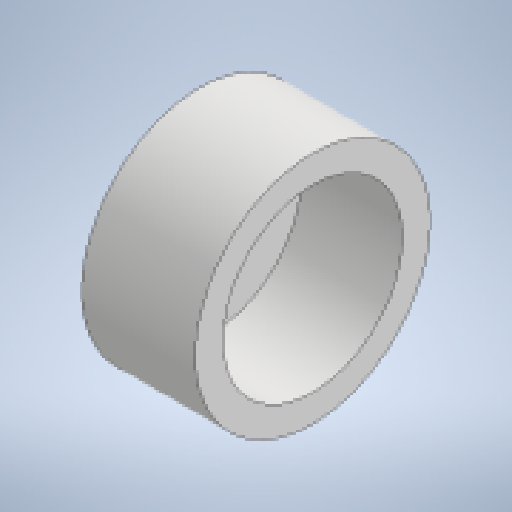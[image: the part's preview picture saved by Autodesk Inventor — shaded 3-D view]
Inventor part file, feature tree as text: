
AUTODESK INVENTOR PART (.ipt)
format: ipt  version: 2023 (Build 270158000, 158)  size: 229,888 bytes
history: native  units: mm
features: extrude x4, sketch x4, other x1
ambient origin geometry x8: Origin, YZ Plane, XZ Plane, XY Plane, X Axis, Y Axis, Z Axis, Center Point
bodies: Body1 (feature_tree)
feature tree (9):
  other  "Bryła1"
  extrude  "Wyciągnięcie proste1"  Depth=30.0mm
  extrude  "Wyciągnięcie proste2"  Depth=3.5mm
  extrude  "Wyciągnięcie proste3"  Depth=14.5mm TaperAngle=0.0deg
  extrude  "Wyciągnięcie proste4"  Depth=1.5mm TaperAngle=0.0deg
  sketch  "Szkic1"
  sketch  "Szkic2"
  sketch  "Szkic3"
  sketch  "Szkic4"
